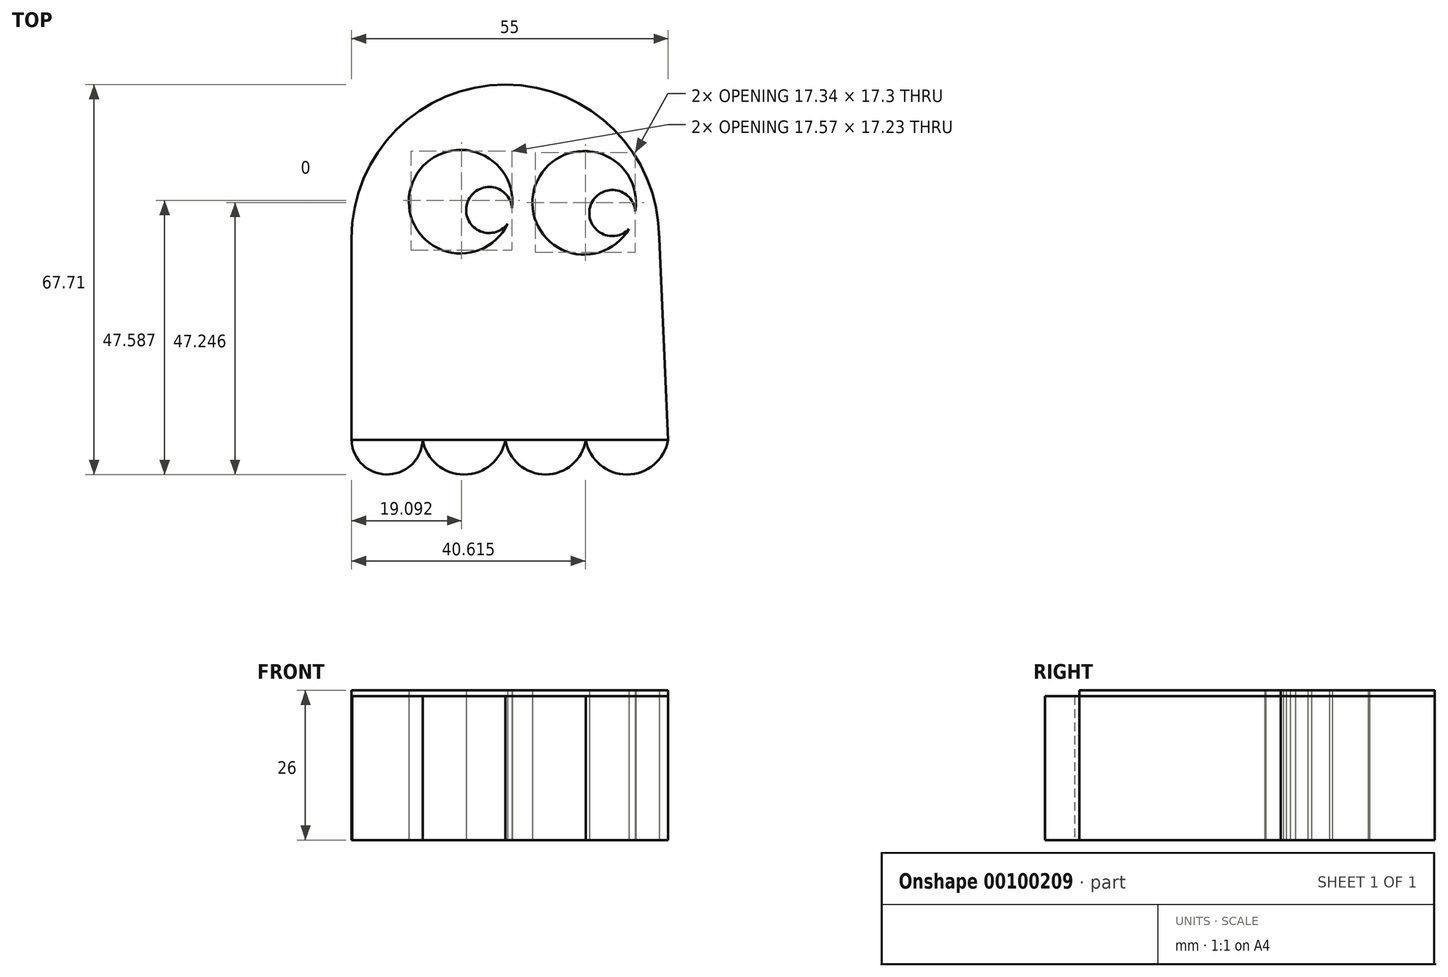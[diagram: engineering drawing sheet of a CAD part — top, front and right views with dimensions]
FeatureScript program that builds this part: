
annotation { "Feature Type Name" : "Feature", "Feature Type Description" : "" }
export const myFeature = defineFeature(function(context is Context, id is Id, definition is map)
    precondition{}
    {
        {
            var Q0;
            Q0=qCreatedBy(makeId("Top.planeOp"),FACE);
            var sketch = newSketch(context, id + "F0", { "sketchPlane" : qUnion([Q0])});
            skArc(sketch, "E0", {"start": v(26.71, 0) * mm, "mid": v(0, 26.71) * mm, "end": v(-26.71, 0) * mm});
            skLineSegment(sketch, "E1", {"start": v(-26.71, 0) * mm, "end": v(-26.71, -35) * mm});
            skLineSegment(sketch, "E2", {"start": v(-26.71, -35) * mm, "end": v(28.29, -35) * mm});
            skLineSegment(sketch, "E3", {"start": v(28.29, -35) * mm, "end": v(26.71, 0) * mm});
            skPoint(sketch, "E4.start.orphan", {"position": v(0, -35) * mm});
            skArc(sketch, "E5", {"start": v(-26.71, -35) * mm, "mid": v(-26.68, -35.43) * mm, "end": v(-26.63, -35.85) * mm});
            skArc(sketch, "E6", {"start": v(-26.71, -35) * mm, "mid": v(-20.54, -41) * mm, "end": v(-14.36, -35) * mm});
            skArc(sketch, "E7", {"start": v(-14.36, -35) * mm, "mid": v(-7.18, -41) * mm, "end": v(0, -35) * mm});
            skArc(sketch, "E8", {"start": v(0, -35) * mm, "mid": v(6.99, -41) * mm, "end": v(13.97, -35) * mm});
            skArc(sketch, "E9", {"start": v(13.97, -35) * mm, "mid": v(21.13, -41) * mm, "end": v(28.29, -35) * mm});
            skArc(sketch, "E10", {"start": v(22.57, 4.7) * mm, "mid": v(5.24, 9.26) * mm, "end": v(21.47, 1.65) * mm});
            skArc(sketch, "E11", {"start": v(1.17, 5.3) * mm, "mid": v(-16.4, 8.9) * mm, "end": v(0.36, 2.5) * mm});
            skArc(sketch, "E12", {"start": v(1.17, 5.3) * mm, "mid": v(-6.66, 6.06) * mm, "end": v(0.36, 2.5) * mm});
            skArc(sketch, "E13", {"start": v(22.57, 4.7) * mm, "mid": v(14.82, 5.78) * mm, "end": v(21.47, 1.65) * mm});
            skSolve(sketch);
        }
        {
            var Q0;
            Q0=makeQuery(id+"F0.imprint","IMPRINT",FACE,{"disambiguationData":[TD([[makeQuery(id+"F0.imprint","IMPRINT",EDGE,{"derivedFrom":sQuery(id+"F0.wireOp",EDGE,"E0")}),1.0]])]});
            var Q1;
            {var subQ1=sQuery(id+"F0.wireOp",EDGE,"E5");Q1=makeQuery(id+"F0.imprint","IMPRINT",FACE,{"disambiguationData":[TD([[makeQuery(id+"F0.imprint","IMPRINT",EDGE,{"derivedFrom":subQ1}),1.0]])]});}
            var Q2;
            {var subQ0=sQuery(id+"F0.wireOp",EDGE,"E7");Q2=makeQuery(id+"F0.imprint","IMPRINT",FACE,{"disambiguationData":[TD([[makeQuery(id+"F0.imprint","IMPRINT",EDGE,{"derivedFrom":subQ0}),1.0]])]});}
            var Q3;
            {var subQ0=sQuery(id+"F0.wireOp",EDGE,"E8");Q3=makeQuery(id+"F0.imprint","IMPRINT",FACE,{"disambiguationData":[TD([[makeQuery(id+"F0.imprint","IMPRINT",EDGE,{"derivedFrom":subQ0}),1.0]])]});}
            var Q4;
            {var subQ0=sQuery(id+"F0.wireOp",EDGE,"E9");Q4=makeQuery(id+"F0.imprint","IMPRINT",FACE,{"disambiguationData":[TD([[makeQuery(id+"F0.imprint","IMPRINT",EDGE,{"derivedFrom":subQ0}),1.0]])]});}
            extrude(context, id + "F1", {"entities" : qUnion([Q0, Q1, Q2, Q3, Q4]), "depth" : 25 * mm});
        }
        {
            var Q0;
            Q0=makeQuery(id+"F0.imprint","IMPRINT",FACE,{"disambiguationData":[TD([[makeQuery(id+"F0.imprint","IMPRINT",EDGE,{"derivedFrom":sQuery(id+"F0.wireOp",EDGE,"E12")}),1.0]])]});
            var Q1;
            Q1=makeQuery(id+"F0.imprint","IMPRINT",FACE,{"disambiguationData":[TD([[makeQuery(id+"F0.imprint","IMPRINT",EDGE,{"derivedFrom":sQuery(id+"F0.wireOp",EDGE,"E13")}),1.0]])]});
            extrude(context, id + "F2", {"entities" : qUnion([Q0, Q1]), "depth" : 26 * mm});
        }
    });
